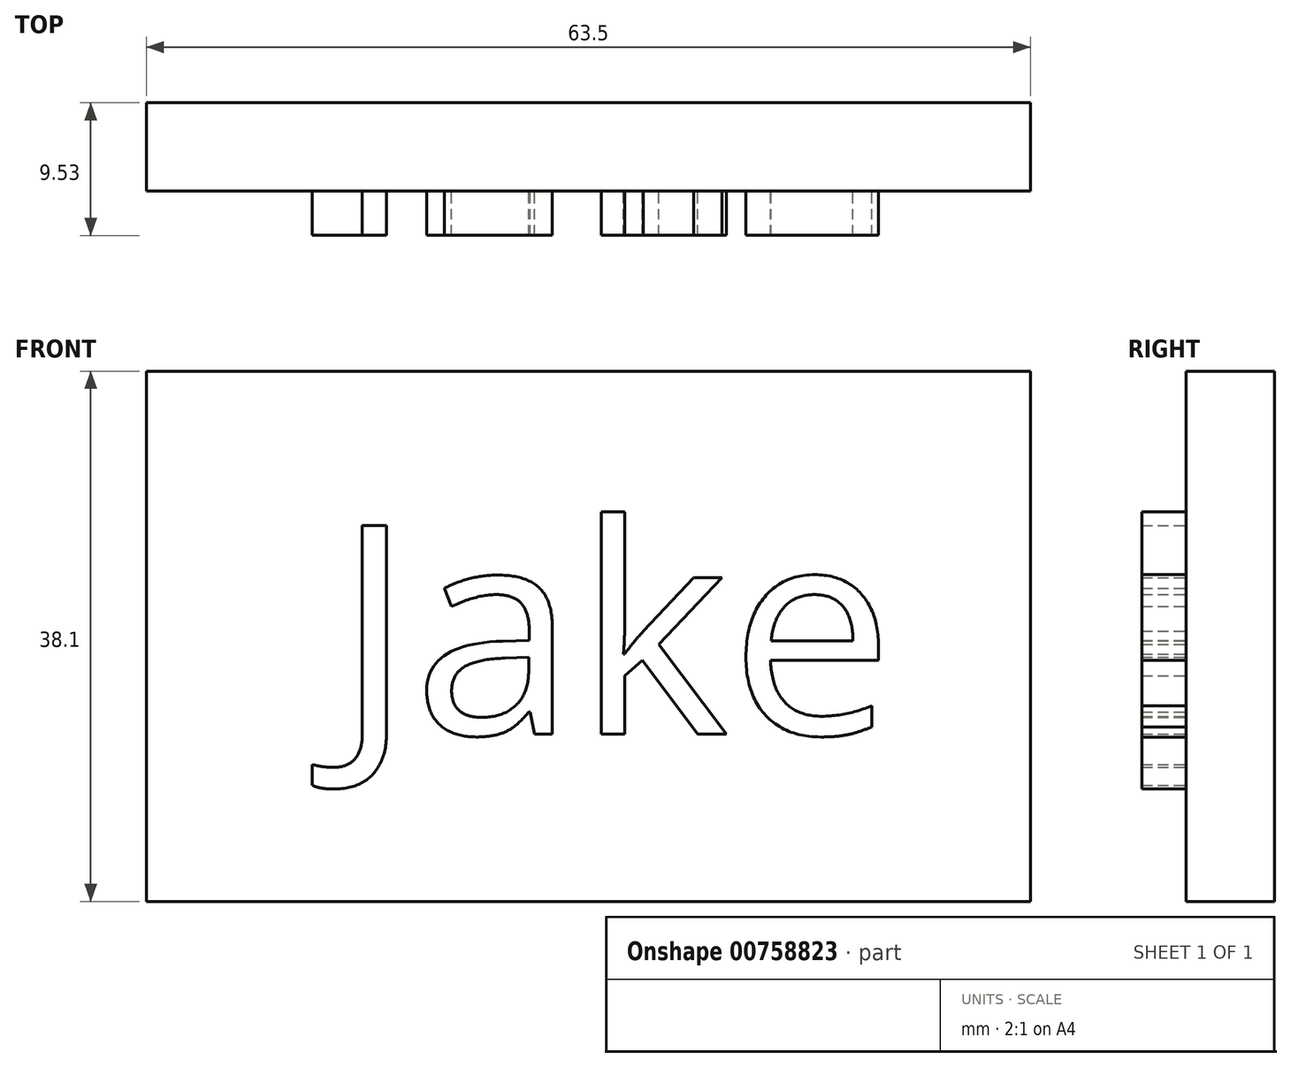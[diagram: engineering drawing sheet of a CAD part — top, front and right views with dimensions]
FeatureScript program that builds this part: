
annotation { "Feature Type Name" : "Feature", "Feature Type Description" : "" }
export const myFeature = defineFeature(function(context is Context, id is Id, definition is map)
    precondition{}
    {
        {
            var Q0;
            Q0=qCreatedBy(makeId("Front.planeOp"),FACE);
            var sketch = newSketch(context, id + "F0", { "sketchPlane" : qUnion([Q0])});
            skLineSegment(sketch, "E0.bottom", {"start": v(0, 0) * mm, "end": v(63.5, 0) * mm});
            skLineSegment(sketch, "E0.top", {"start": v(0, 38.1) * mm, "end": v(63.5, 38.1) * mm});
            skLineSegment(sketch, "E0.left", {"start": v(0, 0) * mm, "end": v(0, 38.1) * mm});
            skLineSegment(sketch, "E0.right", {"start": v(63.5, 0) * mm, "end": v(63.5, 38.1) * mm});
            skSolve(sketch);
        }
        {
            var Q0;
            Q0=makeQuery(id+"F0.imprint","IMPRINT",FACE,{"disambiguationData":[TD([[makeQuery(id+"F0.imprint","IMPRINT",EDGE,{"derivedFrom":sQuery(id+"F0.wireOp",EDGE,"E0.bottom")}),1.0]])]});
            extrude(context, id + "F1", {"entities" : qUnion([Q0]), "depth" : 6.35 * mm, "offsetDistance" : 25.4 * mm});
        }
        {
            var Q0;
            Q0=makeQuery(id+"F1.opExtrude","CAP_FACE",FACE,{"disambiguationData":[OSD([sQuery(id+"F0.wireOp",EDGE,"E0.bottom"),sQuery(id+"F0.wireOp",EDGE,"E0.top"),sQuery(id+"F0.wireOp",EDGE,"E0.left"),sQuery(id+"F0.wireOp",EDGE,"E0.right")])],"isStart":false});
            var sketch = newSketch(context, id + "F2", { "sketchPlane" : qUnion([Q0])});
            skText(sketch, "E1", { "text": "Jake ", "fontName": "OpenSans-Regular.ttf"});
            const initialGuessF2  = {"E1": [0.01356, 0.01202, 1, 0, 0.01513]};
            skSetInitialGuess(sketch, initialGuessF2);
            skSolve(sketch);
        }
        {
            var Q0;
            Q0 = qSketchRegion(id + "F2", true);
            extrude(context, id + "F3", {"entities" : qUnion([Q0]), "operationType" : NewBodyOperationType.ADD, "depth" : 3.17 * mm, "offsetDistance" : 25.4 * mm});
        }
    });
